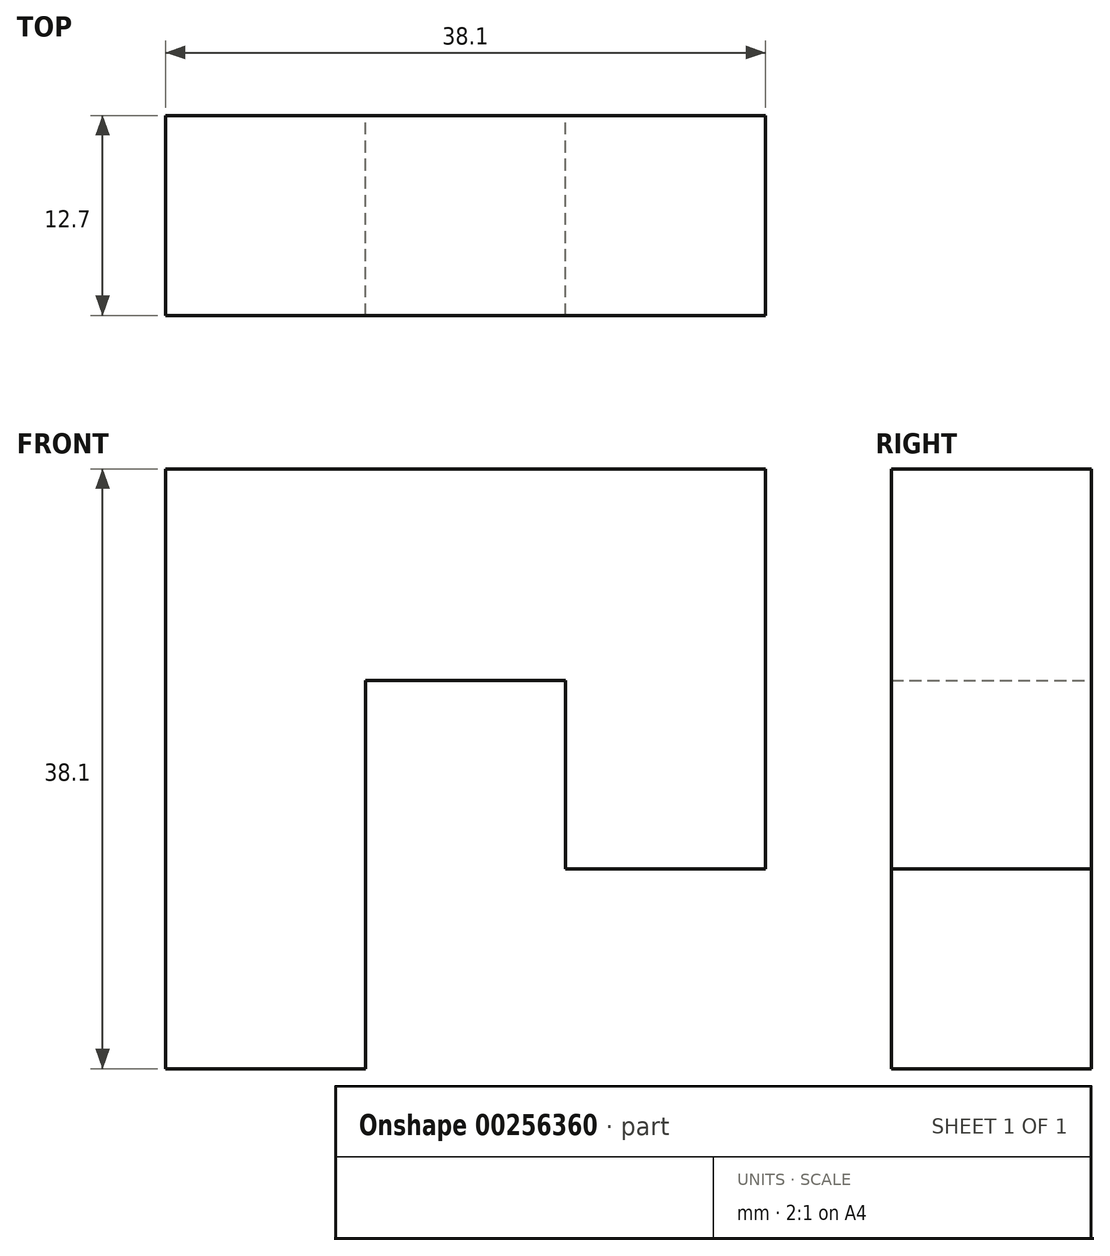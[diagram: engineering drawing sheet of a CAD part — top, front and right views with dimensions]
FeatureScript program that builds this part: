
annotation { "Feature Type Name" : "Feature", "Feature Type Description" : "" }
export const myFeature = defineFeature(function(context is Context, id is Id, definition is map)
    precondition{}
    {
        {
            var Q0;
            Q0=qCreatedBy(makeId("Front.planeOp"),FACE);
            var sketch = newSketch(context, id + "F0", { "sketchPlane" : qUnion([Q0])});
            skLineSegment(sketch, "E0", {"start": v(0, 0) * mm, "end": v(0, 38.1) * mm});
            skLineSegment(sketch, "E1", {"start": v(0, 38.1) * mm, "end": v(38.1, 38.1) * mm});
            skLineSegment(sketch, "E2", {"start": v(38.1, 38.1) * mm, "end": v(38.1, 12.7) * mm});
            skLineSegment(sketch, "E3", {"start": v(38.1, 12.7) * mm, "end": v(25.4, 12.7) * mm});
            skLineSegment(sketch, "E4", {"start": v(25.4, 12.7) * mm, "end": v(25.4, 24.66) * mm});
            skLineSegment(sketch, "E5", {"start": v(25.4, 24.66) * mm, "end": v(12.7, 24.66) * mm});
            skLineSegment(sketch, "E6", {"start": v(12.7, 24.66) * mm, "end": v(12.7, 0) * mm});
            skLineSegment(sketch, "E7", {"start": v(12.7, 0) * mm, "end": v(0, 0) * mm});
            skSolve(sketch);
        }
        {
            var Q0;
            Q0=makeQuery(id+"F0.imprint","IMPRINT",FACE,{"disambiguationData":[TD([[makeQuery(id+"F0.imprint","IMPRINT",EDGE,{"derivedFrom":sQuery(id+"F0.wireOp",EDGE,"E0")}),-1.0]])]});
            extrude(context, id + "F1", {"entities" : qUnion([Q0]), "depth" : 12.7 * mm});
        }
    });
